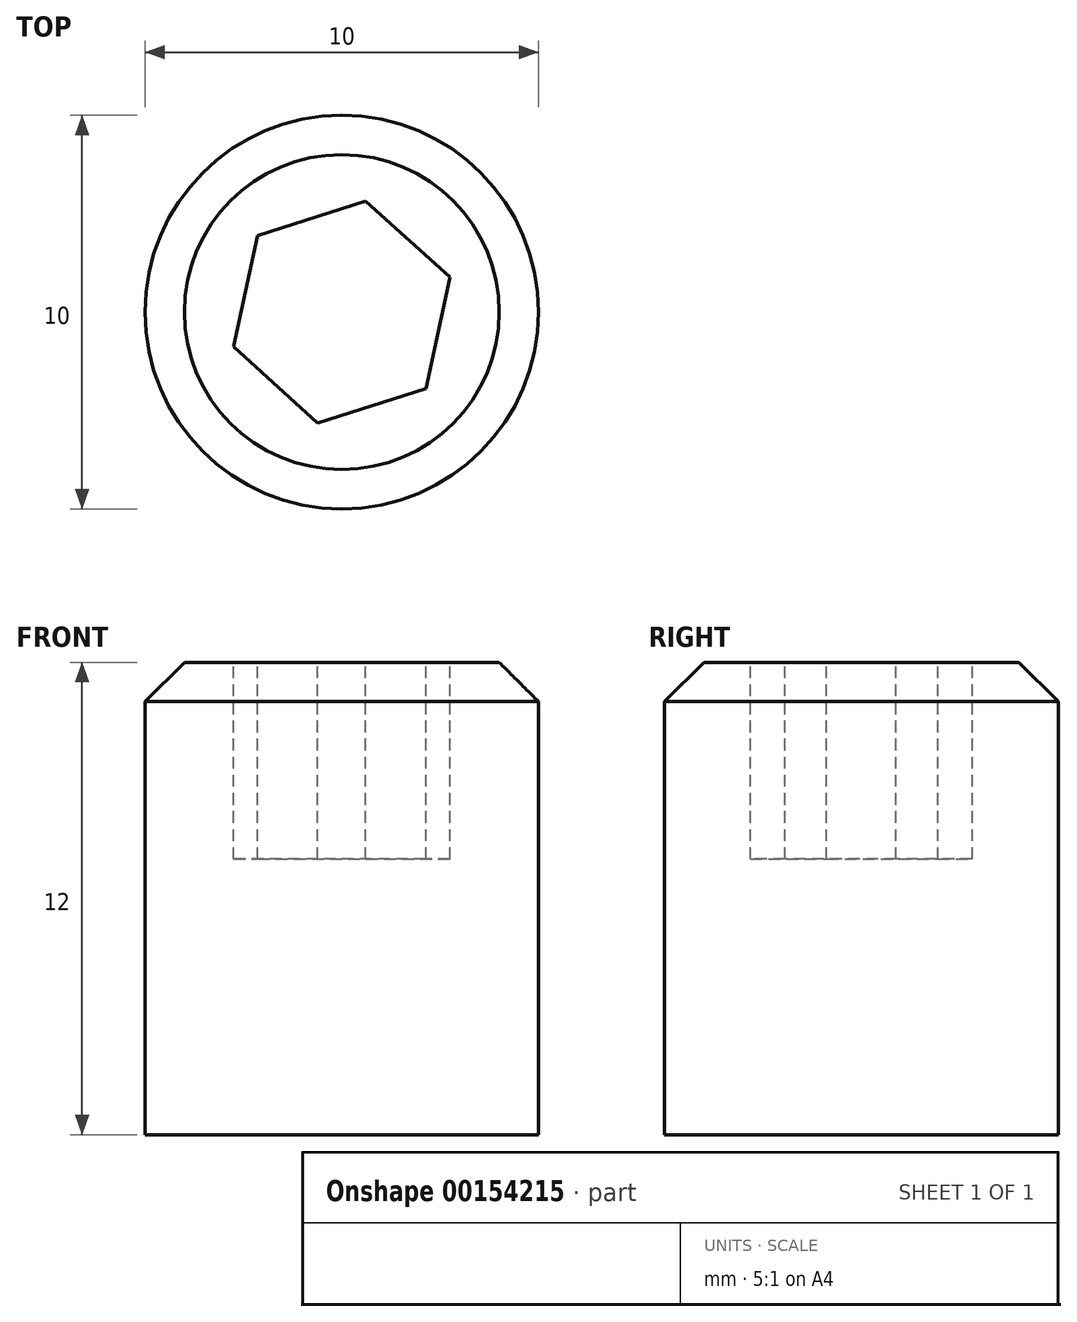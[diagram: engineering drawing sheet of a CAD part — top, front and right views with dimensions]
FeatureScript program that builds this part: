
annotation { "Feature Type Name" : "Feature", "Feature Type Description" : "" }
export const myFeature = defineFeature(function(context is Context, id is Id, definition is map)
    precondition{}
    {
        {
            var Q0;
            Q0=qCreatedBy(makeId("Top.planeOp"),FACE);
            var sketch = newSketch(context, id + "F0", { "sketchPlane" : qUnion([Q0])});
            skCircle(sketch, "E0", {"center": v(0, 0) * mm, "radius": 5 * mm});
            skSolve(sketch);
        }
        {
            var Q0;
            Q0 = qSketchRegion(id + "F0", true);
            extrude(context, id + "F1", {"entities" : qUnion([Q0]), "depth" : 12 * mm});
        }
        {
            var Q0;
            Q0=makeQuery(id+"F1.opExtrude","CAP_FACE",FACE,{"disambiguationData":[OSD([sQuery(id+"F0.wireOp",EDGE,"E0")])],"isStart":false});
            var sketch = newSketch(context, id + "F2", { "sketchPlane" : qUnion([Q0])});
            skCircle(sketch, "E1.cCircle", {"center": v(0, 0) * mm, "radius": 2.5 * mm, "construction": true});
            skLineSegment(sketch, "E1.0", {"start": v(2.75, 0.88) * mm, "end": v(2.14, -1.94) * mm});
            skLineSegment(sketch, "E1.1", {"start": v(2.14, -1.94) * mm, "end": v(-0.61, -2.82) * mm});
            skLineSegment(sketch, "E1.2", {"start": v(-0.61, -2.82) * mm, "end": v(-2.75, -0.88) * mm});
            skLineSegment(sketch, "E1.3", {"start": v(-2.75, -0.88) * mm, "end": v(-2.14, 1.94) * mm});
            skLineSegment(sketch, "E1.4", {"start": v(-2.14, 1.94) * mm, "end": v(0.61, 2.82) * mm});
            skLineSegment(sketch, "E1.5", {"start": v(0.61, 2.82) * mm, "end": v(2.75, 0.88) * mm});
            skPoint(sketch, "E1.0.midPoint", {"position": v(2.44, -0.53) * mm});
            skSolve(sketch);
        }
        {
            var Q0;
            Q0 = qSketchRegion(id + "F2", true);
            extrude(context, id + "F3", {"entities" : qUnion([Q0]), "operationType" : NewBodyOperationType.REMOVE, "oppositeDirection" : true, "depth" : 5 * mm});
        }
        {
            var Q0;
            Q0=makeQuery(id+"F1.opExtrude","CAP_EDGE",EDGE,{"disambiguationData":[OSD([sQuery(id+"F0.wireOp",EDGE,"E0")])],"isStart":false});
            chamfer(context, id + "F4", {"entities" : qUnion([Q0]), "width" : 1 * mm, "tangentPropagation" : true});
        }
    });
